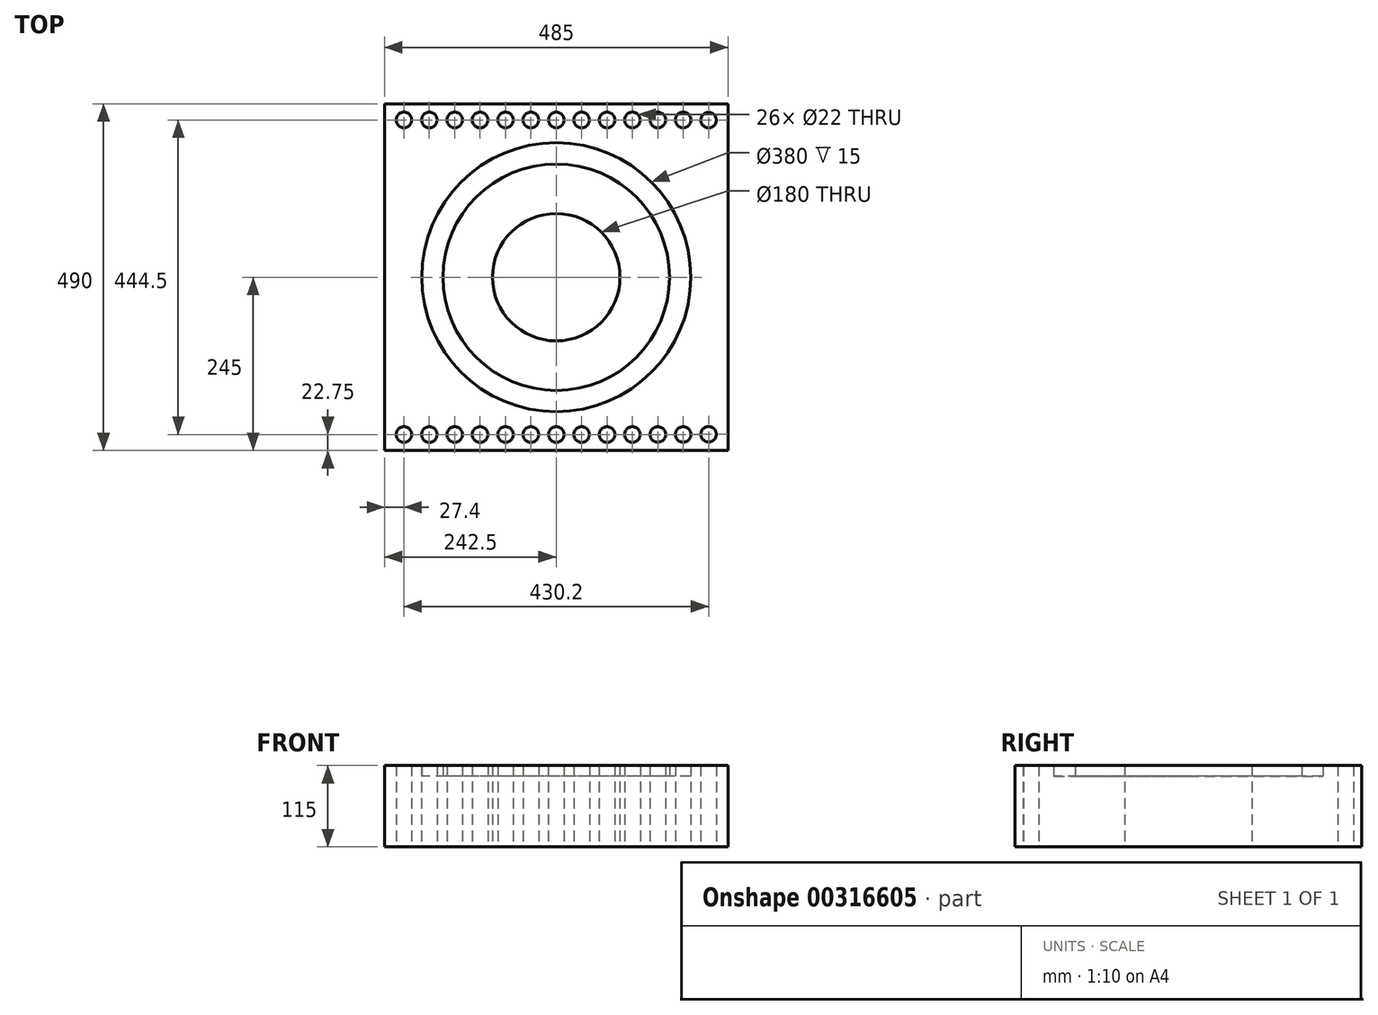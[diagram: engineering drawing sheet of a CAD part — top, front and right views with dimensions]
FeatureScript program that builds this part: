
annotation { "Feature Type Name" : "Feature", "Feature Type Description" : "" }
export const myFeature = defineFeature(function(context is Context, id is Id, definition is map)
    precondition{}
    {
        {
            var Q0;
            Q0=qCreatedBy(makeId("Top.planeOp"),FACE);
            var sketch = newSketch(context, id + "F0", { "sketchPlane" : qUnion([Q0])});
            skLineSegment(sketch, "E0.bottom", {"start": v(242.5, -245) * mm, "end": v(-242.5, -245) * mm});
            skLineSegment(sketch, "E0.top", {"start": v(242.5, 245) * mm, "end": v(-242.5, 245) * mm});
            skLineSegment(sketch, "E0.left", {"start": v(242.5, -245) * mm, "end": v(242.5, 245) * mm});
            skLineSegment(sketch, "E0.right", {"start": v(-242.5, -245) * mm, "end": v(-242.5, 245) * mm});
            skPoint(sketch, "E0.middle", {"position": v(0, 0) * mm});
            skCircle(sketch, "E1", {"center": v(0, 0) * mm, "radius": 190 * mm});
            skCircle(sketch, "E2", {"center": v(0, 0) * mm, "radius": 160 * mm});
            skCircle(sketch, "E3", {"center": v(0, 0) * mm, "radius": 90 * mm});
            skLineSegment(sketch, "E4", {"start": v(0, 0) * mm, "end": v(0, -245) * mm});
            skCircle(sketch, "E5.MirrorC", {"center": v(-35.85, 222.25) * mm, "radius": 11 * mm});
            skCircle(sketch, "E6.MirrorC", {"center": v(0, 222.25) * mm, "radius": 11 * mm});
            skCircle(sketch, "E7.MirrorC", {"center": v(35.85, 222.25) * mm, "radius": 11 * mm});
            skCircle(sketch, "E8.MirrorC", {"center": v(71.7, 222.25) * mm, "radius": 11 * mm});
            skCircle(sketch, "E9.MirrorC", {"center": v(107.55, 222.25) * mm, "radius": 11 * mm});
            skCircle(sketch, "E10.MirrorC", {"center": v(143.4, 222.22) * mm, "radius": 11 * mm});
            skCircle(sketch, "E11.MirrorC", {"center": v(179.25, 222.22) * mm, "radius": 11 * mm});
            skCircle(sketch, "E12.MirrorC", {"center": v(215.1, 221.96) * mm, "radius": 11 * mm});
            skCircle(sketch, "E13.MirrorC", {"center": v(-71.7, 222.25) * mm, "radius": 11 * mm});
            skCircle(sketch, "E14.MirrorC", {"center": v(-107.55, 222.25) * mm, "radius": 11 * mm});
            skCircle(sketch, "E15.MirrorC", {"center": v(-143.4, 222.25) * mm, "radius": 11 * mm});
            skCircle(sketch, "E16.MirrorC", {"center": v(-179.25, 222.25) * mm, "radius": 11 * mm});
            skCircle(sketch, "E17.MirrorC", {"center": v(-215.1, 222.25) * mm, "radius": 11 * mm});
            skCircle(sketch, "E18.MirrorC", {"center": v(-35.85, -222.25) * mm, "radius": 11 * mm});
            skCircle(sketch, "E19.MirrorC", {"center": v(35.85, -222.25) * mm, "radius": 11 * mm});
            skCircle(sketch, "E20.MirrorC", {"center": v(-215.1, -222.25) * mm, "radius": 11 * mm});
            skCircle(sketch, "E21.MirrorC", {"center": v(-143.4, -222.25) * mm, "radius": 11 * mm});
            skCircle(sketch, "E22.MirrorC", {"center": v(71.7, -222.25) * mm, "radius": 11 * mm});
            skCircle(sketch, "E23.MirrorC", {"center": v(143.4, -222.22) * mm, "radius": 11 * mm});
            skCircle(sketch, "E24.MirrorC", {"center": v(107.55, -222.25) * mm, "radius": 11 * mm});
            skCircle(sketch, "E25.MirrorC", {"center": v(-107.55, -222.25) * mm, "radius": 11 * mm});
            skCircle(sketch, "E26.MirrorC", {"center": v(0, -222.25) * mm, "radius": 11 * mm});
            skCircle(sketch, "E27.MirrorC", {"center": v(215.1, -221.96) * mm, "radius": 11 * mm});
            skCircle(sketch, "E28.MirrorC", {"center": v(-71.7, -222.25) * mm, "radius": 11 * mm});
            skCircle(sketch, "E29.MirrorC", {"center": v(179.25, -222.22) * mm, "radius": 11 * mm});
            skCircle(sketch, "E30.MirrorC", {"center": v(-179.25, -222.25) * mm, "radius": 11 * mm});
            skSolve(sketch);
        }
        {
            var Q0;
            Q0=makeQuery(id+"F0.imprint","IMPRINT",FACE,{"disambiguationData":[TD([[makeQuery(id+"F0.imprint","IMPRINT",EDGE,{"derivedFrom":sQuery(id+"F0.wireOp",EDGE,"E0.bottom")}),-1.0]])]});
            extrude(context, id + "F1", {"entities" : qUnion([Q0]), "depth" : 115 * mm});
        }
        {
            var Q0;
            Q0=makeQuery(id+"F0.imprint","IMPRINT",FACE,{"disambiguationData":[TD([[makeQuery(id+"F0.imprint","IMPRINT",EDGE,{"derivedFrom":sQuery(id+"F0.wireOp",EDGE,"E2")}),1.0]])]});
            extrude(context, id + "F2", {"entities" : qUnion([Q0]), "operationType" : NewBodyOperationType.ADD, "depth" : 115 * mm});
        }
        {
            var Q0;
            Q0=makeQuery(id+"F0.imprint","IMPRINT",FACE,{"disambiguationData":[TD([[makeQuery(id+"F0.imprint","IMPRINT",EDGE,{"derivedFrom":sQuery(id+"F0.wireOp",EDGE,"E1")}),1.0]])]});
            extrude(context, id + "F3", {"entities" : qUnion([Q0]), "operationType" : NewBodyOperationType.ADD, "depth" : 100 * mm});
        }
    });
